# Revit family: Lagur Home
name_source: partatom
category: Plumbing Fixtures
units: mm (PartAtom-declared; Revit-internal decimal feet)

## family parameters
Always vertical = No
Cut with Voids When Loaded = No
OmniClass Number = 23.65.50.11.11.14
OmniClass Title = Water Softeners
Part Type = Normal
Room Calculation Point = No
Round Connector Dimension = Use Diameter
Shared = No
Work Plane-Based = No

## types (1)
- DN20
    Default Elevation = 0 mm  [stored 0 ft]
    HW Connection = No
    IP Rating = IP66
    Manufacturer = Lagur A/S
    Model = Lagur Home
    Thread = 3/4" RG.
    Thread dimension in mm = 19 mm
    URL = https://lagur.dk
    Uniclass2015Code = Ss_55_70
    Uniclass2015Description = Water distribution and supply system
    Vent Connection = No
    Version = 1.0
    Waste Connection = No
    Watt = 14 W
    Weight = 2.35 kg
    X = 330 mm
    Y = 63 mm  [stored 0.206693 ft]
    x = 29 mm

note: [stored X ft] marks values corroborated as IEEE doubles in the binary element streams (Revit-internal decimal feet)

## geometry (parser evidence)
native form markers: Sweep x2
no freeform markers — native parametric forms only
